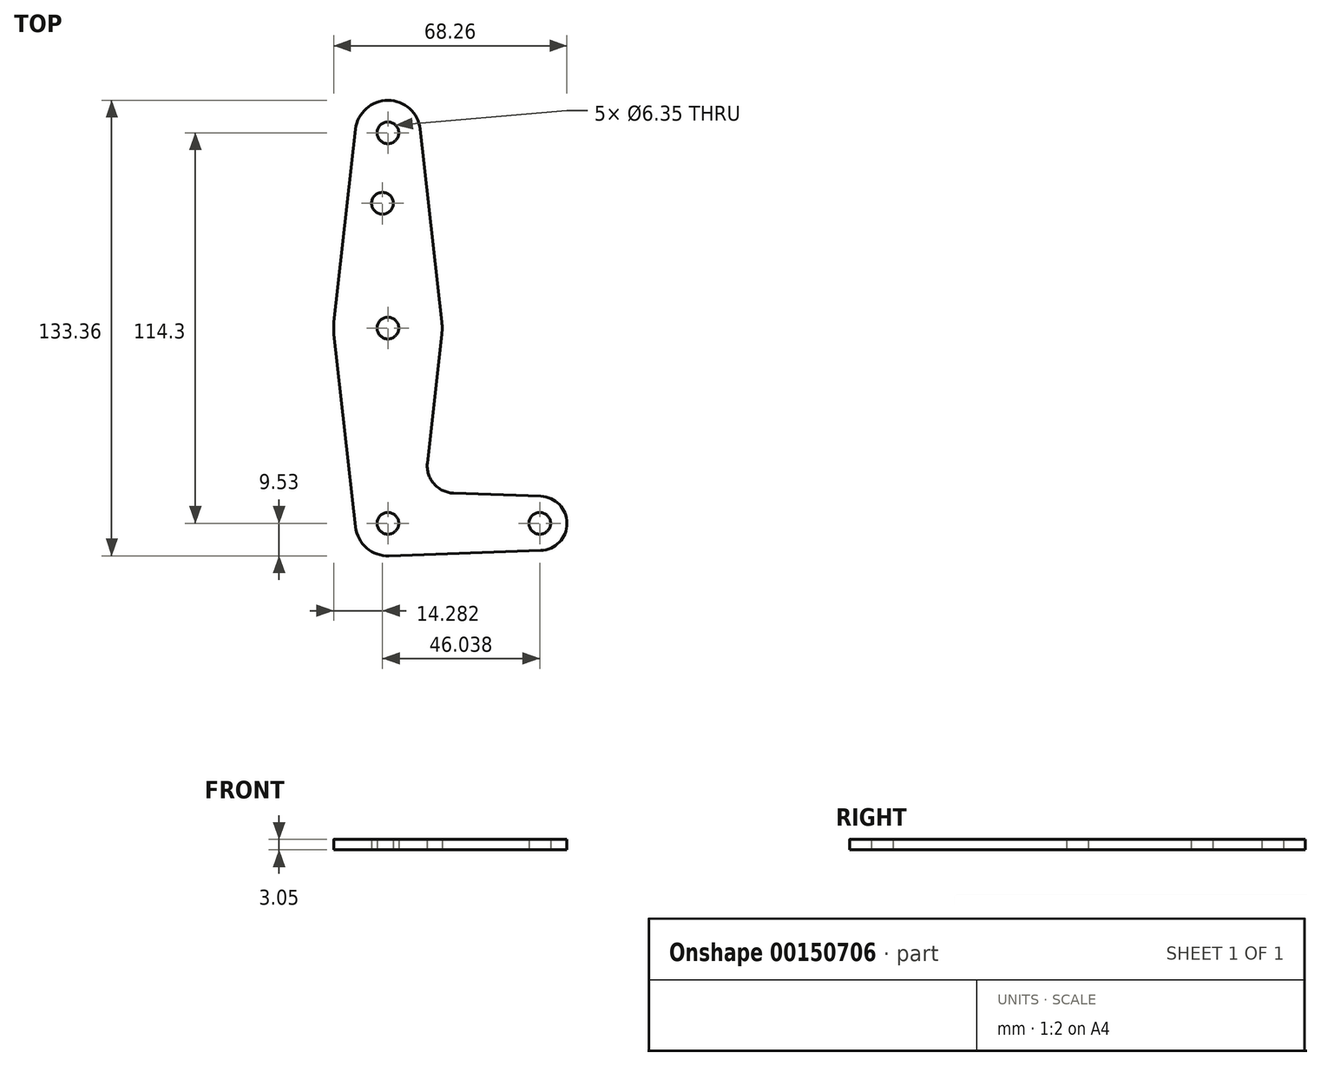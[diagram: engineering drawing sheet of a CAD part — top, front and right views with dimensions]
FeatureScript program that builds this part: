
annotation { "Feature Type Name" : "Feature", "Feature Type Description" : "" }
export const myFeature = defineFeature(function(context is Context, id is Id, definition is map)
    precondition{}
    {
        {
            var Q0;
            Q0=qCreatedBy(makeId("Top.planeOp"),FACE);
            var sketch = newSketch(context, id + "F0", { "sketchPlane" : qUnion([Q0])});
            skLineSegment(sketch, "E0", {"start": v(0, 114.3) * mm, "end": v(0, 0) * mm, "construction": true});
            skLineSegment(sketch, "E1", {"start": v(0, 0) * mm, "end": v(44.45, 0) * mm, "construction": true});
            skCircle(sketch, "E2", {"center": v(0, 114.3) * mm, "radius": 9.53 * mm});
            skCircle(sketch, "E3", {"center": v(0, 57.15) * mm, "radius": 15.88 * mm});
            skCircle(sketch, "E4", {"center": v(0, 0) * mm, "radius": 9.53 * mm});
            skLineSegment(sketch, "E5", {"start": v(-9.47, 115.36) * mm, "end": v(-15.78, 58.91) * mm});
            skLineSegment(sketch, "E6", {"start": v(9.47, 115.36) * mm, "end": v(15.78, 58.91) * mm});
            skCircle(sketch, "E7", {"center": v(44.45, 0) * mm, "radius": 7.94 * mm});
            skLineSegment(sketch, "E8", {"start": v(19.18, 8.85) * mm, "end": v(44.73, 7.93) * mm});
            skLineSegment(sketch, "E9", {"start": v(0.34, -9.52) * mm, "end": v(44.73, -7.93) * mm});
            skCircle(sketch, "E10", {"center": v(0, 114.3) * mm, "radius": 3.18 * mm});
            skCircle(sketch, "E11", {"center": v(0, 57.15) * mm, "radius": 3.18 * mm});
            skCircle(sketch, "E12", {"center": v(-1.59, 93.68) * mm, "radius": 3.18 * mm});
            skCircle(sketch, "E13", {"center": v(0, 0) * mm, "radius": 3.18 * mm});
            skCircle(sketch, "E14", {"center": v(44.45, 0) * mm, "radius": 3.18 * mm});
            skLineSegment(sketch, "E15", {"start": v(-9.47, -1.06) * mm, "end": v(-15.78, 55.39) * mm});
            skLineSegment(sketch, "E16", {"start": v(15.78, 55.39) * mm, "end": v(11.56, 17.67) * mm});
            skArc(sketch, "E17.filletArc", {"start": v(11.56, 17.67) * mm, "mid": v(13.44, 11.6) * mm, "end": v(19.18, 8.85) * mm});
            skSolve(sketch);
        }
        {
            var Q0;
            Q0=makeQuery(id+"F0.imprint","IMPRINT",FACE,{"disambiguationData":[TD([[makeQuery(id+"F0.imprint","IMPRINT",EDGE,{"derivedFrom":sQuery(id+"F0.wireOp",EDGE,"E10")}),-1.0]])]});
            var Q1;
            {var subQ1=sQuery(id+"F0.wireOp",EDGE,"E5");Q1=makeQuery(id+"F0.imprint","IMPRINT",FACE,{"disambiguationData":[TD([[makeQuery(id+"F0.imprint","IMPRINT",EDGE,{"derivedFrom":subQ1}),1.0]])]});}
            var Q2;
            Q2=makeQuery(id+"F0.imprint","IMPRINT",FACE,{"disambiguationData":[TD([[makeQuery(id+"F0.imprint","IMPRINT",EDGE,{"derivedFrom":sQuery(id+"F0.wireOp",EDGE,"E11")}),-1.0]])]});
            var Q3;
            {var subQ0=sQuery(id+"F0.wireOp",EDGE,"E8");Q3=makeQuery(id+"F0.imprint","IMPRINT",FACE,{"disambiguationData":[TD([[makeQuery(id+"F0.imprint","IMPRINT",EDGE,{"derivedFrom":subQ0}),-1.0]])]});}
            var Q4;
            Q4=makeQuery(id+"F0.imprint","IMPRINT",FACE,{"disambiguationData":[TD([[makeQuery(id+"F0.imprint","IMPRINT",EDGE,{"derivedFrom":sQuery(id+"F0.wireOp",EDGE,"E13")}),-1.0]])]});
            var Q5;
            Q5=makeQuery(id+"F0.imprint","IMPRINT",FACE,{"disambiguationData":[TD([[makeQuery(id+"F0.imprint","IMPRINT",EDGE,{"derivedFrom":sQuery(id+"F0.wireOp",EDGE,"E14")}),-1.0]])]});
            extrude(context, id + "F1", {"entities" : qUnion([Q0, Q1, Q2, Q3, Q4, Q5]), "depth" : 3.05 * mm});
        }
    });
